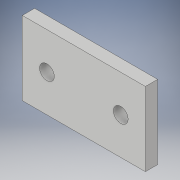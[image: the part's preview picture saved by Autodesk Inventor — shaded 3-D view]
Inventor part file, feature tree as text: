
AUTODESK INVENTOR PART (.ipt)
format: ipt  version: 2017 (Build 210142000, 142)  size: 101,376 bytes
history: native  units: in
note: dims shown in document units (in); Inventor stores cm internally (conversion verified against a paired STEP export)
features: sketch x2, extrude x1, hole x1
ambient origin geometry x8: Origin, YZ Plane, XZ Plane, XY Plane, X Axis, Y Axis, Z Axis, Center Point
bodies: Solid1 (feature_tree)
feature tree (4):
  extrude  "Extrusion1"  Depth=1.5in
  hole  "Hole1"  [1 undecoded]
  sketch  "Sketch1"  dims[d0=2.5in d1=1.5in]
  sketch  "Sketch2"  dims[d2=0.25in d3=0.0in d4=0.5in d5=0.5in d6=180.0deg d7=0.3in d8=0.75in d9=0.375in d10=0.25in d11=0.5635in d12=1.0in d13=0.8108in]
note: 1 required parameter value undecoded (feature->parameter linkage not recoverable at this tier; creation-order binding heuristic only, values carry confidence <= 0.55)
